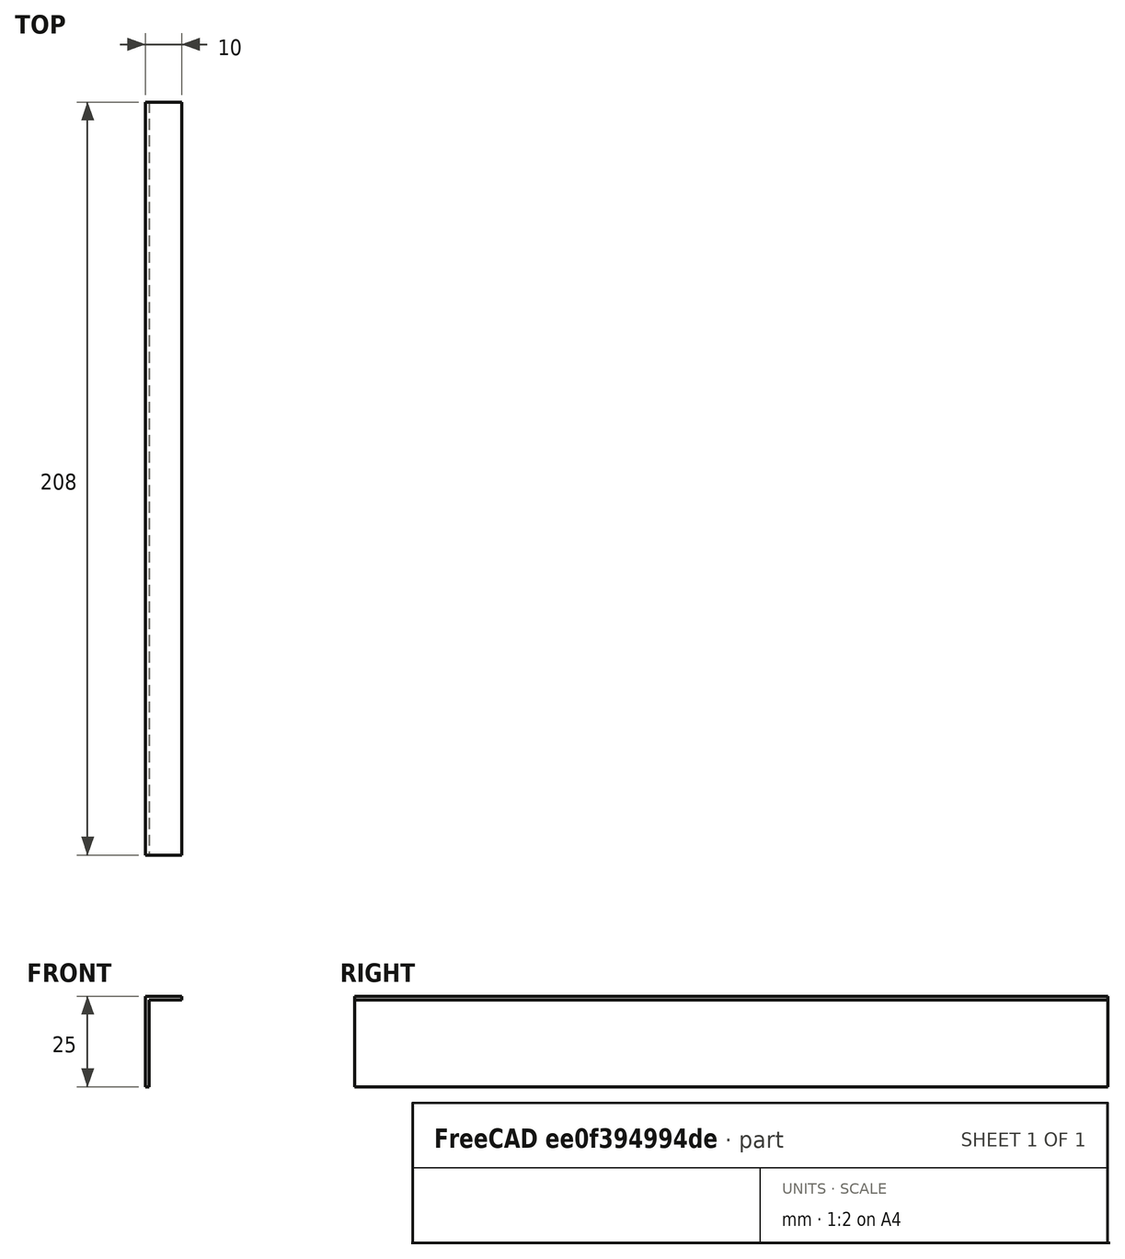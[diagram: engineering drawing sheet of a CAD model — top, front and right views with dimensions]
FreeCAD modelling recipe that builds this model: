
FCSTD DOCUMENT  (FreeCAD 0.21R33694 (Git))
Label: baguette-info-tirettes-lb
License: Creative Commons Attribution 3.0
LicenseURL: http://en.wikipedia.org/wiki/Public_domain
objects: Sketcher::SketchObject×1, PartDesign::Pad×1, PartDesign::Body×1
note: 4 computed .brp shape members not serialized (recipe doc carries the construction recipe); baked Part::Feature solids carry a one-line shape summary decoded from their .brp

FEATURE [Sketcher::SketchObject] Sketch
  FullyConstrained = true
  MapMode = 5
  Placement = pos=(0,0,0) rot=(1,0,0;1.5708rad)
  Support = -> [XZ_Plane]
  sketch-geometry (6):
    g0: LineSegment StartX=9 StartY=0 StartZ=0 EndX=0 EndY=0 EndZ=0
    g1: LineSegment StartX=0 StartY=0 StartZ=0 EndX=0 EndY=-24 EndZ=0
    g2: LineSegment StartX=0 StartY=-24 StartZ=0 EndX=-1 EndY=-24 EndZ=0
    g3: LineSegment StartX=-1 StartY=-24 StartZ=0 EndX=-1 EndY=1 EndZ=0
    g4: LineSegment StartX=-1 StartY=1 StartZ=0 EndX=9 EndY=1 EndZ=0
    g5: LineSegment StartX=9 StartY=1 StartZ=0 EndX=9 EndY=0 EndZ=0
  constraints (17):
    c: PointOnObject(g0,g-1)
    c: Coincident(g0,g-1)
    c: Coincident(g0,g1)
    c: PointOnObject(g1,g-2)
    c: Coincident(g1,g2)
    c: Horizontal(g2)
    c: Coincident(g2,g3)
    c: Vertical(g3)
    c: Coincident(g3,g4)
    c: Horizontal(g4)
    c: Coincident(g4,g5)
    c: Coincident(g5,g0)
    c: Vertical(g5)
    c: DistanceY(g5,g5) = 1
    c: DistanceX(g2,g2) = 1
    c: DistanceX(g4,g4) = 10
    c: DistanceY(g3,g3) = 25
FEATURE [PartDesign::Pad] Pad
  Direction = (0,-1,-2e-16)
  Length = 208
  Length2 = 10
  Placement = pos=(0,0,0) rot=(1,0,0;1.5708rad)
  Profile = -> Sketch
  ReferenceAxis = -> Sketch [N_Axis]
  Type = 0
FEATURE [PartDesign::Body] Body
  Group = -> [Sketch,Pad]
  Origin = -> Origin
  Tip = -> Pad
